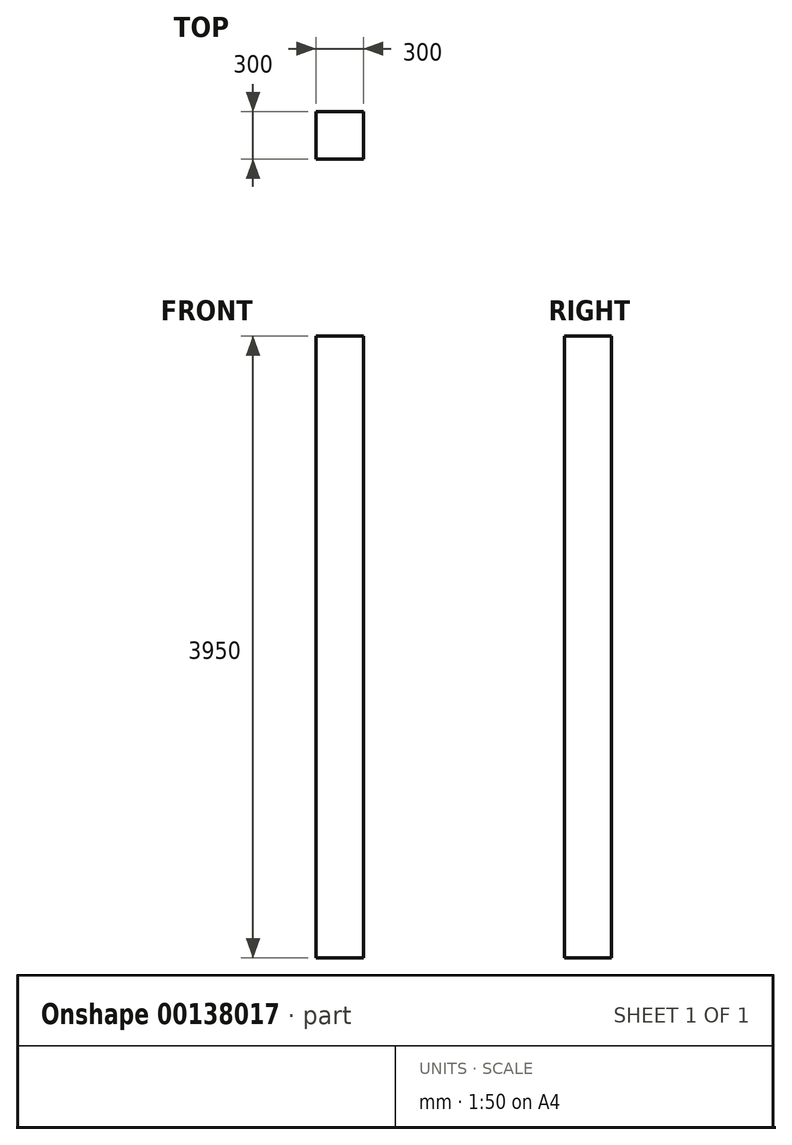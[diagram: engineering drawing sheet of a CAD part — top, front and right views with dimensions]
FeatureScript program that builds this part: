
annotation { "Feature Type Name" : "Feature", "Feature Type Description" : "" }
export const myFeature = defineFeature(function(context is Context, id is Id, definition is map)
    precondition{}
    {
        {
            var Q0;
            Q0=qCreatedBy(makeId("Top.planeOp"),FACE);
            var sketch = newSketch(context, id + "F0", { "sketchPlane" : qUnion([Q0])});
            skLineSegment(sketch, "E0.bottom", {"start": v(150, -150) * mm, "end": v(-150, -150) * mm});
            skLineSegment(sketch, "E0.top", {"start": v(150, 150) * mm, "end": v(-150, 150) * mm});
            skLineSegment(sketch, "E0.left", {"start": v(150, -150) * mm, "end": v(150, 150) * mm});
            skLineSegment(sketch, "E0.right", {"start": v(-150, -150) * mm, "end": v(-150, 150) * mm});
            skPoint(sketch, "E0.middle", {"position": v(0, 0) * mm});
            skSolve(sketch);
        }
        {
            var Q0;
            Q0=makeQuery(id+"F0.imprint","IMPRINT",FACE,{"disambiguationData":[TD([[makeQuery(id+"F0.imprint","IMPRINT",EDGE,{"derivedFrom":sQuery(id+"F0.wireOp",EDGE,"E0.bottom")}),-1.0]])]});
            extrude(context, id + "F1", {"entities" : qUnion([Q0]), "depth" : 3950 * mm});
        }
    });
